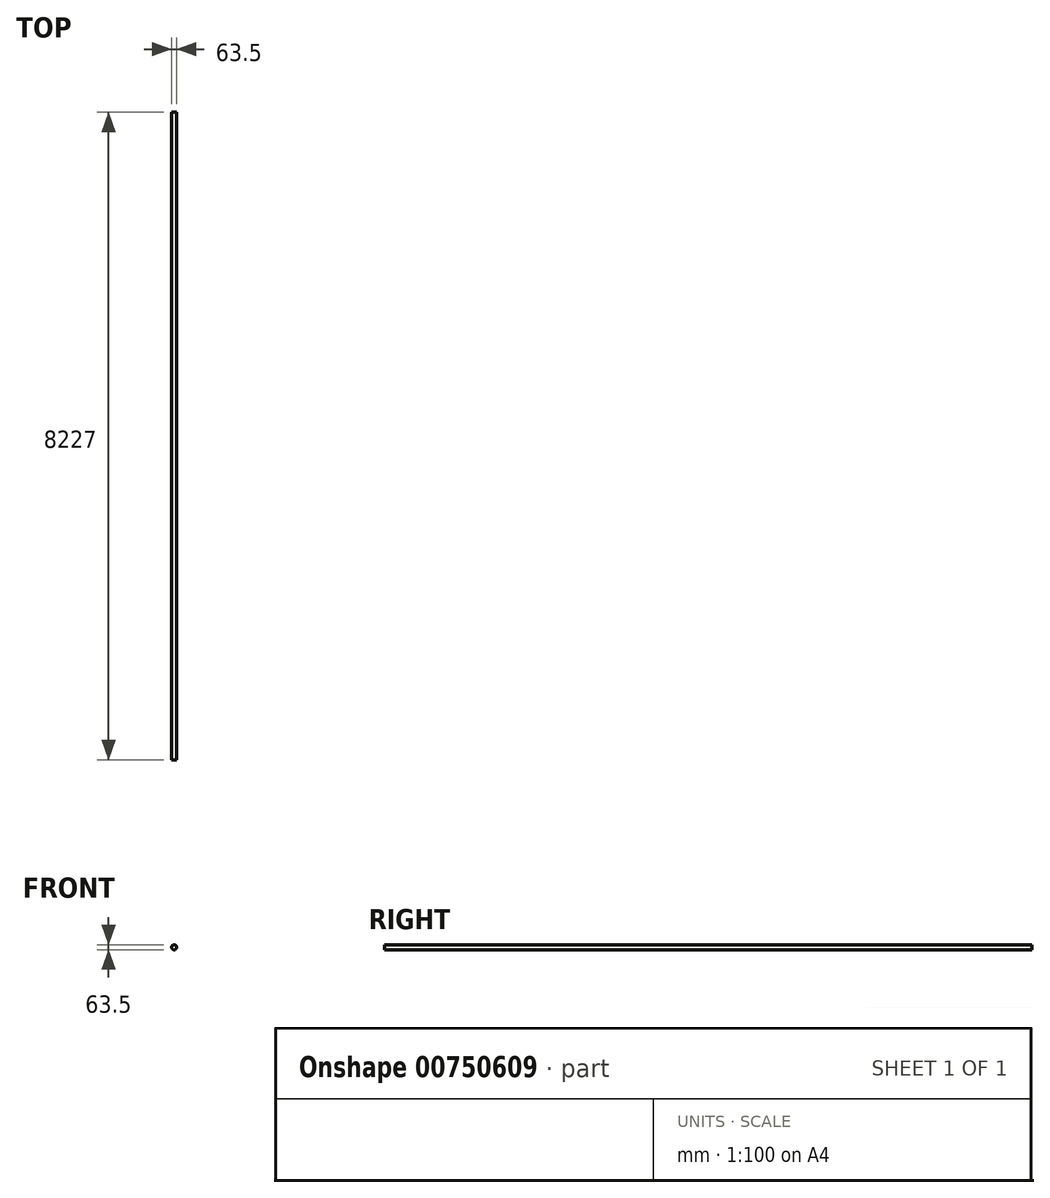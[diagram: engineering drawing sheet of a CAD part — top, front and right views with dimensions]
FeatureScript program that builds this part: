
annotation { "Feature Type Name" : "Feature", "Feature Type Description" : "" }
export const myFeature = defineFeature(function(context is Context, id is Id, definition is map)
    precondition{}
    {
        {
            var Q0;
            Q0=qCreatedBy(makeId("Front.planeOp"),FACE);
            var sketch = newSketch(context, id + "F0", { "sketchPlane" : qUnion([Q0])});
            skCircle(sketch, "E0", {"center": v(0, 0) * mm, "radius": 31.75 * mm});
            skSolve(sketch);
        }
        {
            var Q0;
            Q0=qSketchRegion(id+"F0",true);
            extrude(context, id + "F1", {"entities" : qUnion([Q0]), "depth" : 8227 * mm, "offsetDistance" : 25.4 * mm});
        }
    });
